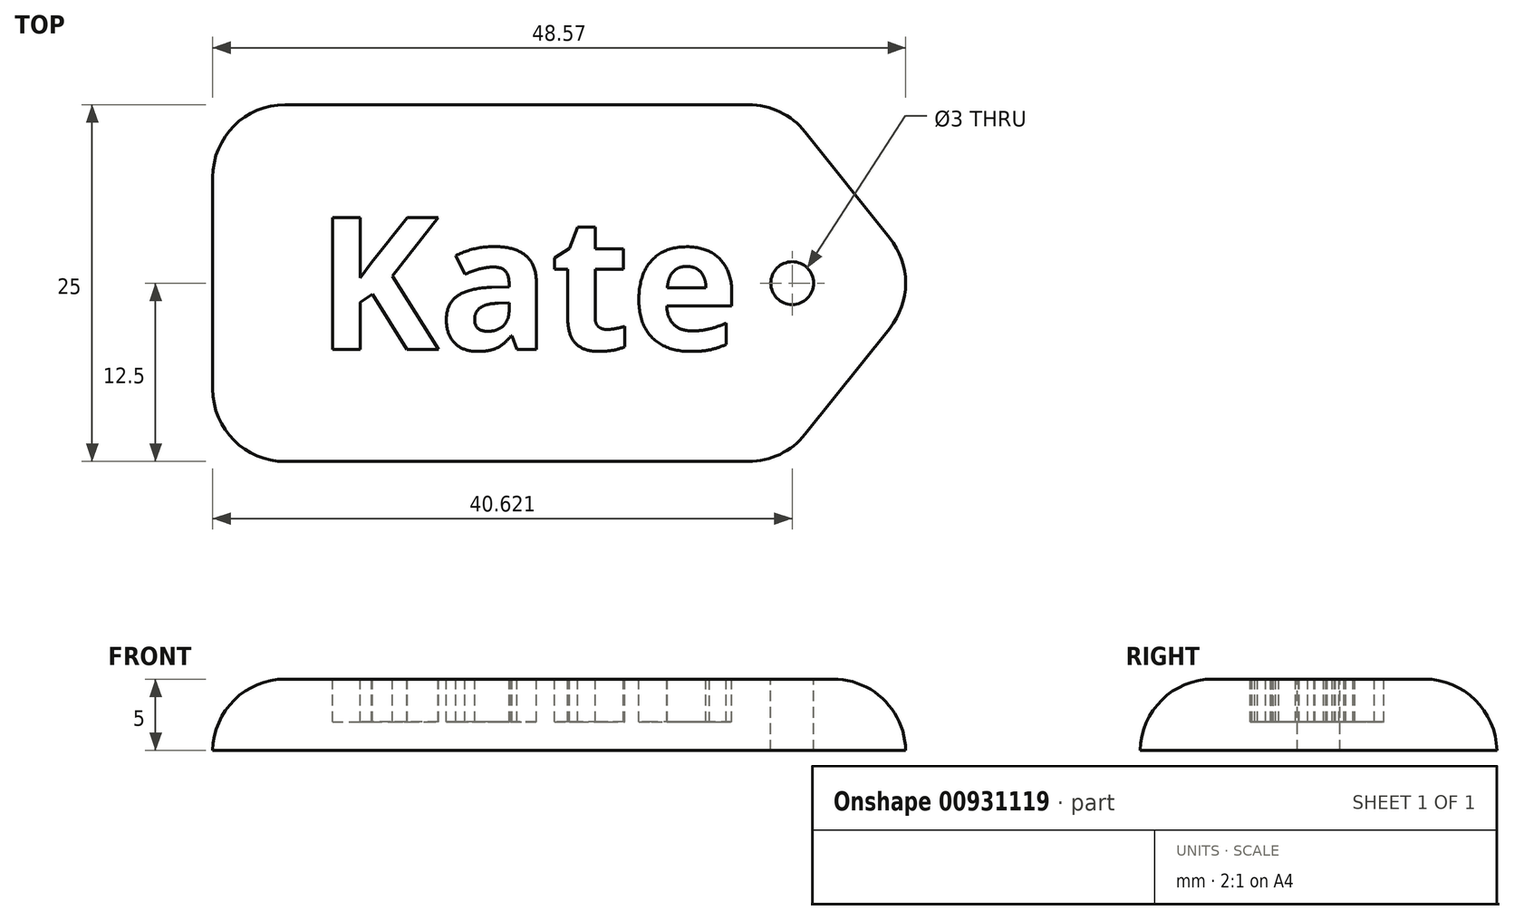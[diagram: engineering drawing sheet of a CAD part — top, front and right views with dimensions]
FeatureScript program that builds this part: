
annotation { "Feature Type Name" : "Feature", "Feature Type Description" : "" }
export const myFeature = defineFeature(function(context is Context, id is Id, definition is map)
    precondition{}
    {
        {
            var Q0;
            Q0=qCreatedBy(makeId("Top.planeOp"),FACE);
            var sketch = newSketch(context, id + "F0", { "sketchPlane" : qUnion([Q0])});
            skLineSegment(sketch, "E0.bottom", {"start": v(20, -12.5) * mm, "end": v(-20, -12.5) * mm});
            skLineSegment(sketch, "E0.top", {"start": v(20, 12.5) * mm, "end": v(-20, 12.5) * mm});
            skLineSegment(sketch, "E0.right", {"start": v(-20, -12.5) * mm, "end": v(-20, 12.5) * mm});
            skPoint(sketch, "E0.middle", {"position": v(0, 0) * mm});
            skPoint(sketch, "E1", {"position": v(30, 0) * mm});
            skLineSegment(sketch, "E2", {"start": v(20, 12.5) * mm, "end": v(30, 0) * mm});
            skLineSegment(sketch, "E3", {"start": v(20, -12.5) * mm, "end": v(30, 0) * mm});
            skSolve(sketch);
        }
        {
            var Q0;
            Q0=makeQuery(id+"F0.imprint","IMPRINT",FACE,{"disambiguationData":[TD([[makeQuery(id+"F0.imprint","IMPRINT",EDGE,{"derivedFrom":sQuery(id+"F0.wireOp",EDGE,"E0.bottom")}),-1.0]])]});
            extrude(context, id + "F1", {"entities" : qUnion([Q0]), "depth" : 5 * mm, "offsetDistance" : 25.4 * mm});
        }
        {
            var Q0;
            Q0=makeQuery(id+"F1.opExtrude","SWEPT_EDGE",EDGE,{"disambiguationData":[OSD([sQuery(id+"F0.wireOp",EDGE,"E2"),sQuery(id+"F0.wireOp",EDGE,"E3")])]});
            var Q1;
            Q1=makeQuery(id+"F1.opExtrude","SWEPT_EDGE",EDGE,{"disambiguationData":[OSD([sQuery(id+"F0.wireOp",EDGE,"E0.bottom"),sQuery(id+"F0.wireOp",EDGE,"E3")])]});
            fillet(context, id + "F2", {"entities" : qUnion([Q0, Q1]), "radius" : 5.08 * mm, "tangentPropagation" : true, "allowEdgeOverflow" : false});
        }
        {
            var Q0;
            Q0=makeQuery(id+"F1.opExtrude","SWEPT_EDGE",EDGE,{"disambiguationData":[OSD([sQuery(id+"F0.wireOp",EDGE,"E0.top"),sQuery(id+"F0.wireOp",EDGE,"E2")])]});
            fillet(context, id + "F3", {"entities" : qUnion([Q0]), "radius" : 5.08 * mm, "tangentPropagation" : true, "allowEdgeOverflow" : false});
        }
        {
            var Q0;
            Q0=makeQuery(id+"F1.opExtrude","SWEPT_EDGE",EDGE,{"disambiguationData":[OSD([sQuery(id+"F0.wireOp",EDGE,"E0.top"),sQuery(id+"F0.wireOp",EDGE,"E0.right")])]});
            fillet(context, id + "F4", {"entities" : qUnion([Q0]), "radius" : 5.08 * mm, "tangentPropagation" : true, "allowEdgeOverflow" : false});
        }
        {
            var Q0;
            Q0=makeQuery(id+"F1.opExtrude","SWEPT_EDGE",EDGE,{"disambiguationData":[OSD([sQuery(id+"F0.wireOp",EDGE,"E0.bottom"),sQuery(id+"F0.wireOp",EDGE,"E0.right")])]});
            fillet(context, id + "F5", {"entities" : qUnion([Q0]), "radius" : 5.08 * mm, "tangentPropagation" : true, "allowEdgeOverflow" : false});
        }
        {
            var Q0;
            Q0=makeQuery(id+"F1.opExtrude","CAP_FACE",FACE,{"disambiguationData":[OSD([sQuery(id+"F0.wireOp",EDGE,"E0.bottom"),sQuery(id+"F0.wireOp",EDGE,"E0.top"),sQuery(id+"F0.wireOp",EDGE,"E0.right"),sQuery(id+"F0.wireOp",EDGE,"E2"),sQuery(id+"F0.wireOp",EDGE,"E3")])],"isStart":false});
            fillet(context, id + "F6", {"entities" : qUnion([Q0]), "radius" : 5.08 * mm, "tangentPropagation" : true, "allowEdgeOverflow" : false});
        }
        {
            var Q0;
            Q0=makeQuery(id+"F1.opExtrude","CAP_FACE",FACE,{"disambiguationData":[OSD([sQuery(id+"F0.wireOp",EDGE,"E0.bottom"),sQuery(id+"F0.wireOp",EDGE,"E0.top"),sQuery(id+"F0.wireOp",EDGE,"E0.right"),sQuery(id+"F0.wireOp",EDGE,"E2"),sQuery(id+"F0.wireOp",EDGE,"E3")])],"isStart":false});
            var sketch = newSketch(context, id + "F7", { "sketchPlane" : qUnion([Q0])});
            skText(sketch, "E4", { "text": "Kate", "fontName": "OpenSans-Bold.ttf"});
            const initialGuessF7  = {"E4": [-0.01277, -0.00466, 1, 0, 0.00933]};
            skSetInitialGuess(sketch, initialGuessF7);
            skSolve(sketch);
        }
        {
            var Q0;
            Q0 = qSketchRegion(id + "F7", true);
            extrude(context, id + "F8", {"entities" : qUnion([Q0]), "operationType" : NewBodyOperationType.REMOVE, "oppositeDirection" : true, "depth" : 3 * mm, "offsetDistance" : 25.4 * mm});
        }
        {
            var Q0;
            Q0=makeQuery(id+"F7.imprint","IMPRINT",FACE,{"disambiguationData":[TD([[makeQuery(id+"F7.imprint","IMPRINT",EDGE,{"derivedFrom":sQuery(id+"F7.wireOp",EDGE,"E4.sketch_text.stroke-0")}),1.0]])]});
            var sketch = newSketch(context, id + "F9", { "sketchPlane" : qUnion([Q0])});
            skPoint(sketch, "E5", {"position": v(0, 0) * mm});
            skPoint(sketch, "E6", {"position": v(20.62, 0) * mm});
            skSolve(sketch);
        }
        {
            var Q0;
            Q0=sQuery(id+"F9.wireOp",VERTEX,"E6");
            var Q1;
            Q1=makeQuery(id+"F1.opExtrude","SWEPT_BODY",BODY,{"disambiguationData":[OSD([sQuery(id+"F0.wireOp",EDGE,"E0.bottom"),sQuery(id+"F0.wireOp",EDGE,"E0.top"),sQuery(id+"F0.wireOp",EDGE,"E0.right"),sQuery(id+"F0.wireOp",EDGE,"E2"),sQuery(id+"F0.wireOp",EDGE,"E3")])]});
            hole(context, id + "F10", {"style" : HoleStyle.SIMPLE, "endStyle" : HoleEndStyle.THROUGH, "holeDiameter" : 3 * mm, "majorDiameter" : 6.35 * mm, "isTappedThrough" : true, "tappedDepth" : 12.7 * mm, "tapClearance" : 3, "locations" : qUnion([Q0]), "scope" : qUnion([Q1])});
        }
    });
